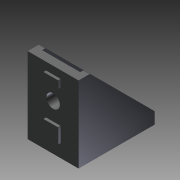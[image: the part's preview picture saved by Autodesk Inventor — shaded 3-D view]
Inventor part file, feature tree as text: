
AUTODESK INVENTOR PART (.ipt)
format: ipt  version: 2016 SP1 (Build 200210100, 210)  size: 219,136 bytes
history: native  units: mm
features: other x42, sketch x10, extrude x7, hole x3
ambient origin geometry x8: Origin, YZ Plane, XZ Plane, XY Plane, X Axis, Y Axis, Z Axis, Center Point
bodies: Solid1 (feature_tree)
feature tree (62):
  extrude  "Extrusion1"  Depth=15.0mm TaperAngle=0.0deg
  extrude  "Extrusion2"  Depth=1.0mm TaperAngle=0.0deg
  extrude  "Extrusion3"  Depth=1.0mm TaperAngle=0.0deg
  hole  "Hole1"  [1 undecoded]
  hole  "Hole2"  [1 undecoded]
  hole  "Hole3"  [1 undecoded]
  extrude  "Extrusion4"  [1 undecoded]
  extrude  "Extrusion5"  [1 undecoded]
  extrude  "Extrusion6"  [1 undecoded]
  extrude  "Extrusion7"  [1 undecoded]
  other  "bracket_to_bolt_XY"
  other  "bracket_to_bolt_YZ"
  other  "bracket_to_bolt_ZX"
  other  "bracket_to_bolt_X"
  other  "bracket_to_bolt_Y"
  other  "bracket_to_bolt_Z"
  other  "bracket_to_bolt_Center"
  other  "bracket_to_dummy_XY"
  other  "bracket_to_dummy_YZ"
  other  "bracket_to_dummy_ZX"
  other  "bracket_to_dummy_X"
  other  "bracket_to_dummy_Y"
  other  "bracket_to_dummy_Z"
  other  "bracket_to_dummy_Center"
  other  "to_bolt_4_7_base_XY"
  other  "to_bolt_4_7_base_YZ"
  other  "to_bolt_4_7_base_ZX"
  other  "to_bolt_4_7_base_X"
  other  "to_bolt_4_7_base_Y"
  other  "to_bolt_4_7_base_Z"
  other  "to_bolt_4_7_base_Center"
  other  "to_bolt_row_4_to_7_XY"
  other  "to_bolt_row_4_to_7_YZ"
  other  "to_bolt_row_4_to_7_ZX"
  other  "to_bolt_row_4_to_7_X"
  other  "to_bolt_row_4_to_7_Y"
  other  "to_bolt_row_4_to_7_Z"
  other  "to_bolt_row_4_to_7_Center"
  other  "to_nut_base_4_7_XY"
  other  "to_nut_base_4_7_YZ"
  other  "to_nut_base_4_7_ZX"
  other  "to_nut_base_4_7_X"
  other  "to_nut_base_4_7_Y"
  other  "to_nut_base_4_7_Z"
  other  "to_nut_base_4_7_Center"
  other  "to_nut_row_4_to_7_XY"
  other  "to_nut_row_4_to_7_YZ"
  other  "to_nut_row_4_to_7_ZX"
  other  "to_nut_row_4_to_7_X"
  other  "to_nut_row_4_to_7_Y"
  other  "to_nut_row_4_to_7_Z"
  other  "to_nut_row_4_to_7_Center"
  sketch  "Sketch_15"
  sketch  "Sketch_16"
  sketch  "Sketch_17"
  sketch  "Sketch4"  dims[d4=2.25mm d5=0.0mm]
  sketch  "Sketch5"  dims[d13=5.3mm d14=6.0mm d15=4.0mm d16=2.0mm d17=90.0deg d18=4.5mm d19=0.0mm]
  sketch  "Sketch6"  dims[d20=5.3mm d21=6.0mm d22=4.0mm d23=2.0mm d24=90.0deg d25=4.5mm d26=0.0mm d27=1.0mm d28=0.0mm]
  sketch  "Sketch_1"  dims[d0=20.0mm d1=0.0mm d2=15.0mm d3=0.0mm]
  sketch  "Sketch_4"  dims[d6=5.3mm d7=6.0mm d8=4.0mm d9=2.0mm d10=90.0deg d11=4.5mm d12=0.0mm]
  sketch  "Sketch_10"  dims[d29=1.0mm d30=0.0mm d31=1.0mm d32=0.0mm]
  sketch  "Sketch_11"  dims[d33=1.0mm d34=0.0mm]
note: 7 required parameter values undecoded (feature->parameter linkage not recoverable at this tier; creation-order binding heuristic only, values carry confidence <= 0.55)
